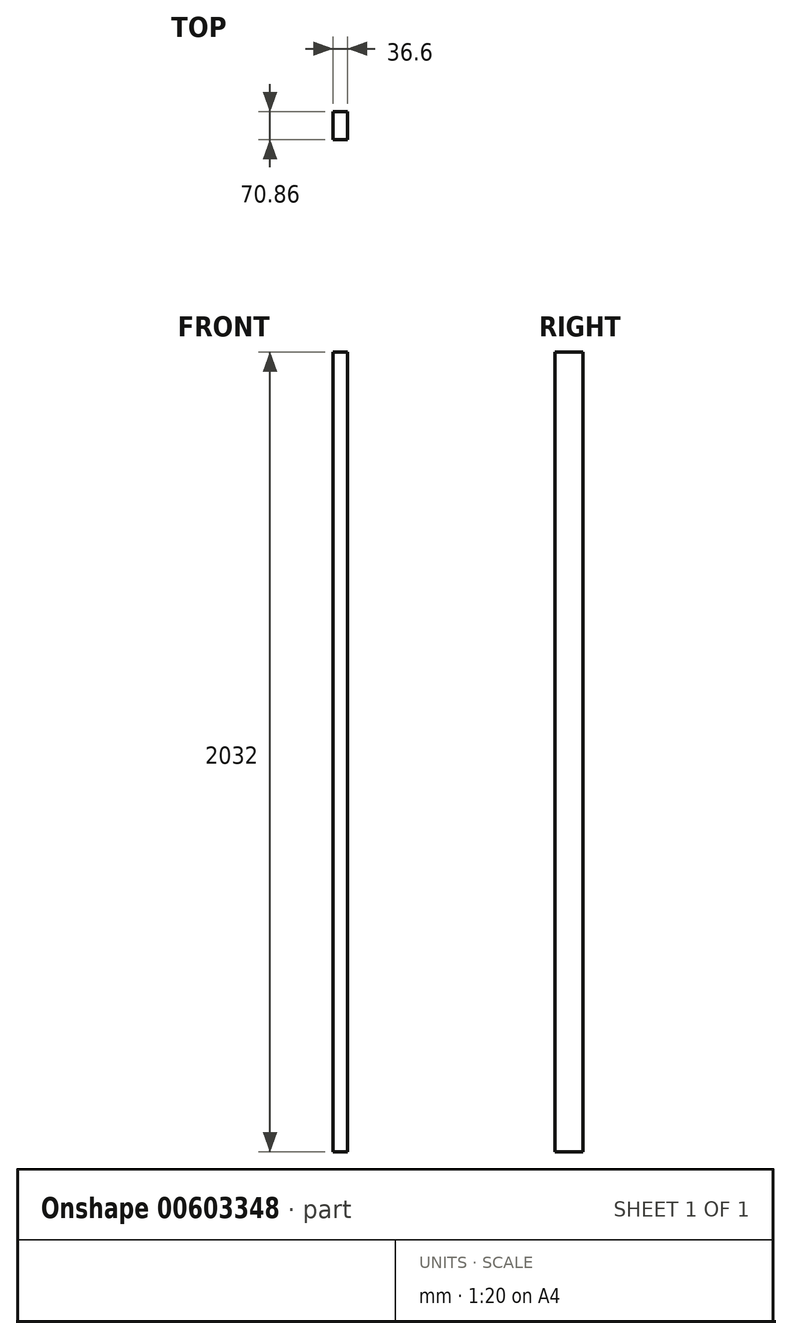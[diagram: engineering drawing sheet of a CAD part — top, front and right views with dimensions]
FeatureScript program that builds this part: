
annotation { "Feature Type Name" : "Feature", "Feature Type Description" : "" }
export const myFeature = defineFeature(function(context is Context, id is Id, definition is map)
    precondition{}
    {
        {
            var Q0;
            Q0=qCreatedBy(makeId("Top.planeOp"),FACE);
            var sketch = newSketch(context, id + "F0", { "sketchPlane" : qUnion([Q0])});
            skLineSegment(sketch, "E0.bottom", {"start": v(18.3, -35.43) * mm, "end": v(-18.3, -35.43) * mm});
            skLineSegment(sketch, "E0.top", {"start": v(18.3, 35.43) * mm, "end": v(-18.3, 35.43) * mm});
            skLineSegment(sketch, "E0.left", {"start": v(18.3, -35.43) * mm, "end": v(18.3, 35.43) * mm});
            skLineSegment(sketch, "E0.right", {"start": v(-18.3, -35.43) * mm, "end": v(-18.3, 35.43) * mm});
            skPoint(sketch, "E0.middle", {"position": v(0, 0) * mm});
            skSolve(sketch);
        }
        {
            var Q0;
            Q0=makeQuery(id+"F0.imprint","IMPRINT",FACE,{"disambiguationData":[TD([[makeQuery(id+"F0.imprint","IMPRINT",EDGE,{"derivedFrom":sQuery(id+"F0.wireOp",EDGE,"E0.bottom")}),-1.0]])]});
            extrude(context, id + "F1", {"entities" : qUnion([Q0]), "depth" : 2032 * mm, "offsetDistance" : 25.4 * mm});
        }
    });
